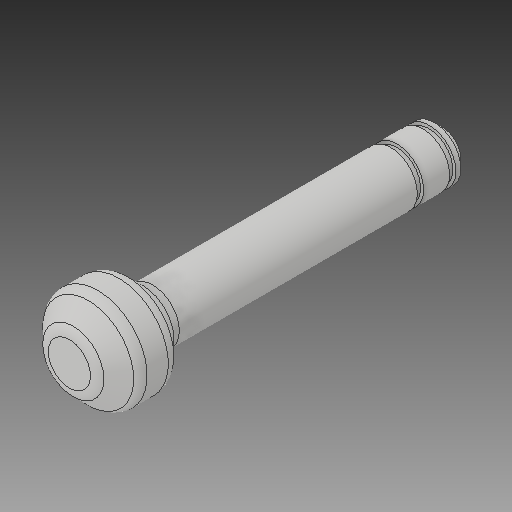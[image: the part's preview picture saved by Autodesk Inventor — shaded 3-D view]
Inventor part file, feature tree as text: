
AUTODESK INVENTOR PART (.ipt)
format: ipt  version: 2017 (Build 210142000, 142)  size: 127,488 bytes
history: native  units: in
note: dims shown in document units (in); Inventor stores cm internally (conversion verified against a paired STEP export)
features: chamfer x1
ambient origin geometry x8: Origin, YZ Plane, XZ Plane, XY Plane, X Axis, Y Axis, Z Axis, Center Point
bodies: Solid1 (feature_tree)
feature tree (1):
  chamfer  "Chamfer1"  [1 undecoded]
note: 1 required parameter value undecoded (feature->parameter linkage not recoverable at this tier; creation-order binding heuristic only, values carry confidence <= 0.55)
